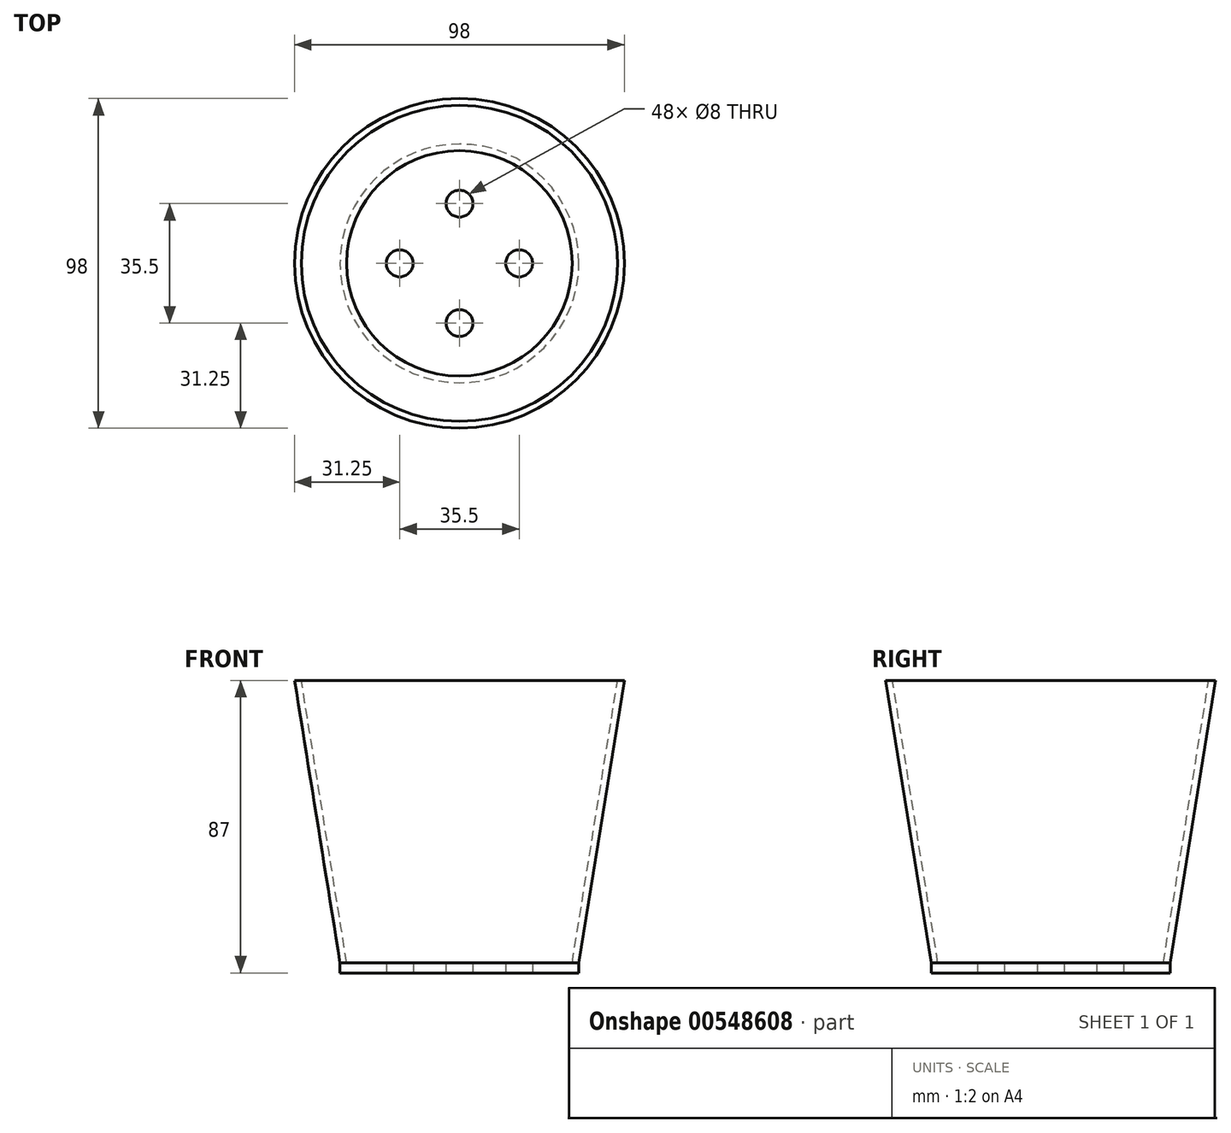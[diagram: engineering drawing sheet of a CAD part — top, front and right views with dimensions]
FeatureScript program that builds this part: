
annotation { "Feature Type Name" : "Feature", "Feature Type Description" : "" }
export const myFeature = defineFeature(function(context is Context, id is Id, definition is map)
    precondition{}
    {
        {
            var Q0;
            Q0=qCreatedBy(makeId("Front.planeOp"),FACE);
            var sketch = newSketch(context, id + "F0", { "sketchPlane" : qUnion([Q0])});
            skLineSegment(sketch, "E0.bottom", {"start": v(0, 0) * mm, "end": v(-35.5, 0) * mm});
            skLineSegment(sketch, "E0.top", {"start": v(0, 3) * mm, "end": v(-35.5, 3) * mm});
            skLineSegment(sketch, "E0.left", {"start": v(0, 0) * mm, "end": v(0, 3) * mm});
            skLineSegment(sketch, "E0.right", {"start": v(-35.5, 0) * mm, "end": v(-35.5, 3) * mm});
            skLineSegment(sketch, "E1", {"start": v(-35.5, 3) * mm, "end": v(-49, 87) * mm});
            skLineSegment(sketch, "E2", {"start": v(-47, 87) * mm, "end": v(-33.5, 3) * mm});
            skLineSegment(sketch, "E3", {"start": v(-49, 87) * mm, "end": v(-47, 87) * mm});
            skLineSegment(sketch, "E4", {"start": v(0, 3) * mm, "end": v(0, 87) * mm});
            skSolve(sketch);
        }
        {
            var Q0;
            {var subQ0=sQuery(id+"F0.wireOp",EDGE,"E1");Q0=makeQuery(id+"F0.imprint","IMPRINT",FACE,{"disambiguationData":[TD([[makeQuery(id+"F0.imprint","IMPRINT",EDGE,{"derivedFrom":subQ0}),-1.0]])]});}
            var Q1;
            Q1=makeQuery(id+"F0.imprint","IMPRINT",FACE,{"disambiguationData":[TD([[makeQuery(id+"F0.imprint","IMPRINT",EDGE,{"derivedFrom":sQuery(id+"F0.wireOp",EDGE,"E0.bottom")}),-1.0]])]});
            var Q2;
            Q2=sQuery(id+"F0.wireOp",EDGE,"E4");
            revolve(context, id + "F1", {"entities" : qUnion([Q0, Q1]), "axis" : qUnion([Q2]), "revolveType" : RevolveType.FULL});
        }
        {
            var Q0;
            Q0=makeQuery(id+"F1.opRevolve","SWEPT_FACE",FACE,{"disambiguationData":[OSD([sQuery(id+"F0.wireOp",EDGE,"E0.bottom")])]});
            var sketch = newSketch(context, id + "F2", { "sketchPlane" : qUnion([Q0])});
            skCircle(sketch, "E5", {"center": v(0, 17.75) * mm, "radius": 4 * mm});
            skCircle(sketch, "E6", {"center": v(17.75, 0) * mm, "radius": 4 * mm});
            skCircle(sketch, "E7", {"center": v(-17.75, 0) * mm, "radius": 4 * mm});
            skCircle(sketch, "E8", {"center": v(0, -17.75) * mm, "radius": 4 * mm});
            skSolve(sketch);
        }
        {
            var Q0;
            Q0 = qSketchRegion(id + "F2", true);
            extrude(context, id + "F3", {"entities" : qUnion([Q0]), "operationType" : NewBodyOperationType.REMOVE, "endBound" : BoundingType.THROUGH_ALL, "oppositeDirection" : true, "depth" : 25.4 * mm, "offsetDistance" : 25.4 * mm});
        }
    });
